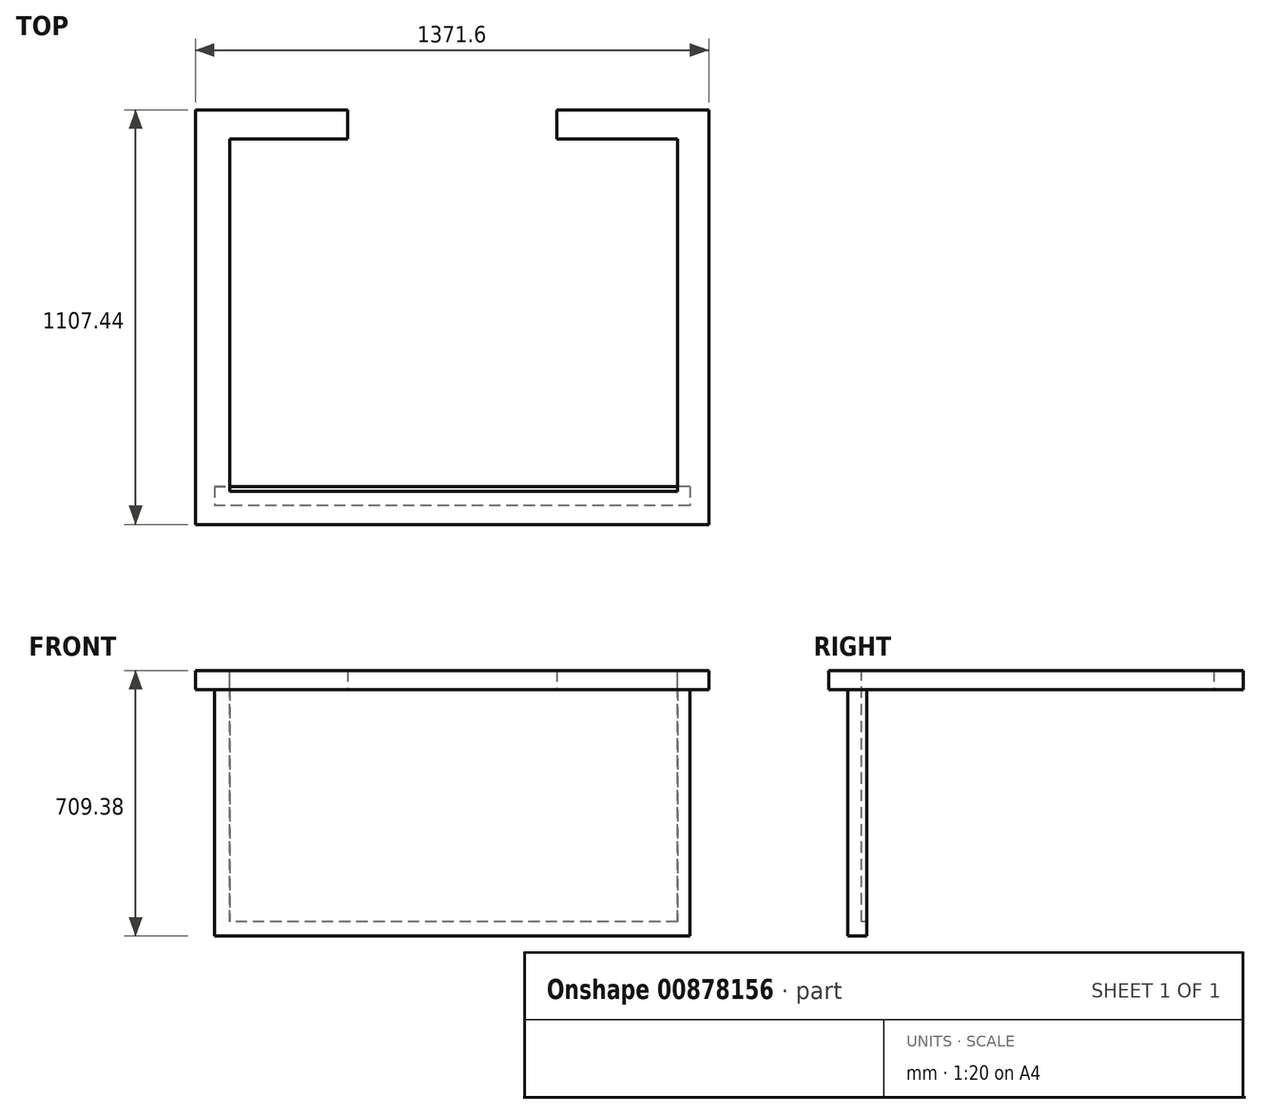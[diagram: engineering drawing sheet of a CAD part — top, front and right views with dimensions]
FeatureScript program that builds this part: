
annotation { "Feature Type Name" : "Feature", "Feature Type Description" : "" }
export const myFeature = defineFeature(function(context is Context, id is Id, definition is map)
    precondition{}
    {
        {
            var Q0;
            Q0=qCreatedBy(makeId("Front.planeOp"),FACE);
            var sketch = newSketch(context, id + "F0", { "sketchPlane" : qUnion([Q0])});
            skLineSegment(sketch, "E0", {"start": v(0, 0) * mm, "end": v(-1270, 0) * mm});
            skLineSegment(sketch, "E1", {"start": v(-1270, 0) * mm, "end": v(-1270, 658.58) * mm});
            skLineSegment(sketch, "E2", {"start": v(-1270, 658.58) * mm, "end": v(-1320.8, 658.58) * mm});
            skLineSegment(sketch, "E3", {"start": v(-1320.8, 658.58) * mm, "end": v(-1320.8, 709.38) * mm});
            skLineSegment(sketch, "E4", {"start": v(-1320.8, 709.38) * mm, "end": v(50.8, 709.38) * mm});
            skLineSegment(sketch, "E5", {"start": v(50.8, 709.38) * mm, "end": v(50.8, 658.58) * mm});
            skLineSegment(sketch, "E6", {"start": v(50.8, 658.58) * mm, "end": v(0, 658.58) * mm});
            skLineSegment(sketch, "E7", {"start": v(0, 658.58) * mm, "end": v(0, 0) * mm});
            skLineSegment(sketch, "E8", {"start": v(0, 658.58) * mm, "end": v(0, 709.38) * mm});
            skLineSegment(sketch, "E9", {"start": v(-1270, 658.58) * mm, "end": v(-1270, 709.38) * mm});
            skSolve(sketch);
        }
        {
            var Q0;
            Q0=makeQuery(id+"F0.imprint","IMPRINT",FACE,{"disambiguationData":[TD([[makeQuery(id+"F0.imprint","IMPRINT",EDGE,{"derivedFrom":sQuery(id+"F0.wireOp",EDGE,"E2")}),-1.0]])]});
            var Q1;
            {var subQ0=sQuery(id+"F0.wireOp",EDGE,"E5");Q1=makeQuery(id+"F0.imprint","IMPRINT",FACE,{"disambiguationData":[TD([[makeQuery(id+"F0.imprint","IMPRINT",EDGE,{"derivedFrom":subQ0}),-1.0]])]});}
            var Q2;
            Q2=makeQuery(id+"F0.imprint","IMPRINT",FACE,{"disambiguationData":[TD([[makeQuery(id+"F0.imprint","IMPRINT",EDGE,{"derivedFrom":sQuery(id+"F0.wireOp",EDGE,"E0")}),-1.0]])]});
            extrude(context, id + "F1", {"entities" : qUnion([Q0, Q1, Q2]), "oppositeDirection" : true, "depth" : 1005.84 * mm, "offsetDistance" : 25.4 * mm});
        }
        {
            var Q0;
            Q0=makeQuery(id+"F1.opExtrude","CAP_FACE",FACE,{"disambiguationData":[OSD([sQuery(id+"F0.wireOp",EDGE,"E0"),sQuery(id+"F0.wireOp",EDGE,"E1"),sQuery(id+"F0.wireOp",EDGE,"E2"),sQuery(id+"F0.wireOp",EDGE,"E3"),sQuery(id+"F0.wireOp",EDGE,"E4"),sQuery(id+"F0.wireOp",EDGE,"E5"),sQuery(id+"F0.wireOp",EDGE,"E6"),sQuery(id+"F0.wireOp",EDGE,"E7")])],"isStart":false});
            var sketch = newSketch(context, id + "F2", { "sketchPlane" : qUnion([Q0])});
            skLineSegment(sketch, "E10", {"start": v(-50.8, 658.58) * mm, "end": v(355.6, 658.58) * mm});
            skLineSegment(sketch, "E11", {"start": v(355.6, 658.58) * mm, "end": v(355.6, 709.38) * mm});
            skLineSegment(sketch, "E12", {"start": v(355.6, 709.38) * mm, "end": v(-50.8, 709.38) * mm});
            skLineSegment(sketch, "E13", {"start": v(-50.8, 709.38) * mm, "end": v(-50.8, 658.58) * mm});
            skLineSegment(sketch, "E14", {"start": v(1320.8, 658.58) * mm, "end": v(914.4, 658.58) * mm});
            skLineSegment(sketch, "E15", {"start": v(914.4, 658.58) * mm, "end": v(914.4, 709.38) * mm});
            skLineSegment(sketch, "E16", {"start": v(914.4, 709.38) * mm, "end": v(1320.8, 709.38) * mm});
            skLineSegment(sketch, "E17", {"start": v(1320.8, 709.38) * mm, "end": v(1320.8, 658.58) * mm});
            skSolve(sketch);
        }
        {
            var Q0;
            {var subQ0=sQuery(id+"F2.wireOp",EDGE,"E15");Q0=makeQuery(id+"F2.imprint","IMPRINT",FACE,{"disambiguationData":[TD([[makeQuery(id+"F2.imprint","IMPRINT",EDGE,{"derivedFrom":subQ0}),-1.0]])]});}
            var Q1;
            {var subQ0=sQuery(id+"F2.wireOp",EDGE,"E11");Q1=makeQuery(id+"F2.imprint","IMPRINT",FACE,{"disambiguationData":[TD([[makeQuery(id+"F2.imprint","IMPRINT",EDGE,{"derivedFrom":subQ0}),1.0]])]});}
            extrude(context, id + "F3", {"entities" : qUnion([Q0, Q1]), "operationType" : NewBodyOperationType.ADD, "depth" : 50.8 * mm, "offsetDistance" : 25.4 * mm});
        }
        {
            var Q0;
            Q0=makeQuery(id+"F1.opExtrude","CAP_FACE",FACE,{"disambiguationData":[OSD([sQuery(id+"F0.wireOp",EDGE,"E0"),sQuery(id+"F0.wireOp",EDGE,"E1"),sQuery(id+"F0.wireOp",EDGE,"E2"),sQuery(id+"F0.wireOp",EDGE,"E3"),sQuery(id+"F0.wireOp",EDGE,"E4"),sQuery(id+"F0.wireOp",EDGE,"E5"),sQuery(id+"F0.wireOp",EDGE,"E6"),sQuery(id+"F0.wireOp",EDGE,"E7")])],"isStart":true});
            var sketch = newSketch(context, id + "F4", { "sketchPlane" : qUnion([Q0])});
            skLineSegment(sketch, "E18", {"start": v(-1320.8, 658.58) * mm, "end": v(50.8, 658.58) * mm});
            skLineSegment(sketch, "E19", {"start": v(50.8, 658.58) * mm, "end": v(50.8, 709.38) * mm});
            skLineSegment(sketch, "E20", {"start": v(50.8, 709.38) * mm, "end": v(-1320.8, 709.38) * mm});
            skLineSegment(sketch, "E21", {"start": v(-1320.8, 709.38) * mm, "end": v(-1320.8, 658.58) * mm});
            skSolve(sketch);
        }
        {
            var Q0;
            Q0 = qSketchRegion(id + "F4", true);
            extrude(context, id + "F5", {"entities" : qUnion([Q0]), "operationType" : NewBodyOperationType.ADD, "depth" : 50.8 * mm, "offsetDistance" : 25.4 * mm});
        }
        {
            var Q0;
            Q0=makeQuery(id+"F5.boolean.opBoolean","MERGE",FACE,{"derivedFrom":[makeQuery(id+"F3.boolean.opBoolean","MERGE",FACE,{"derivedFrom":[makeQuery(id+"F1.opExtrude","SWEPT_FACE",FACE,{"disambiguationData":[OSD([sQuery(id+"F0.wireOp",EDGE,"E4")])]}),makeQuery(id+"F3.opExtrude","SWEPT_FACE",FACE,{"disambiguationData":[OSD([sQuery(id+"F2.wireOp",EDGE,"E12")])]}),makeQuery(id+"F3.opExtrude","SWEPT_FACE",FACE,{"disambiguationData":[OSD([sQuery(id+"F2.wireOp",EDGE,"E16")])]})]}),makeQuery(id+"F5.opExtrude","SWEPT_FACE",FACE,{"disambiguationData":[OSD([sQuery(id+"F4.wireOp",EDGE,"E20")])]})]});
            var sketch = newSketch(context, id + "F6", { "sketchPlane" : qUnion([Q0])});
            skPoint(sketch, "E22.0", {"position": v(50.8, -50.8) * mm});
            skPoint(sketch, "E23.0", {"position": v(0, 0) * mm});
            skSolve(sketch);
        }
        {
            var Q0;
            {var subQ1=sQuery(id+"F2.wireOp",EDGE,"E12");Q0=makeQuery(id+"F6.imprint","IMPRINT",FACE,{"disambiguationData":[TD([[makeQuery(id+"F6.imprint","IMPRINT",EDGE,{"derivedFrom":makeQuery(id+"F3.opExtrude","CAP_EDGE",EDGE,{"disambiguationData":[OSD([subQ1])],"isStart":false})}),-1.0]])]});}
            var sketch = newSketch(context, id + "F7", { "sketchPlane" : qUnion([Q0])});
            skLineSegment(sketch, "E24", {"start": v(-1271.6, 1006.87) * mm, "end": v(0, 1006.87) * mm});
            skLineSegment(sketch, "E25", {"start": v(0, 1006.87) * mm, "end": v(0, 0) * mm});
            skLineSegment(sketch, "E26", {"start": v(0, 0) * mm, "end": v(-1269.46, 0) * mm});
            skLineSegment(sketch, "E27", {"start": v(-1269.46, 0) * mm, "end": v(-1271.6, 1006.87) * mm});
            skSolve(sketch);
        }
        {
            var Q0;
            {var subQ5=sQuery(id+"F7.wireOp",EDGE,"E25");Q0=makeQuery(id+"F7.imprint","IMPRINT",FACE,{"disambiguationData":[TD([[makeQuery(id+"F7.imprint","IMPRINT",EDGE,{"derivedFrom":subQ5}),-1.0]])]});}
            var sketch = newSketch(context, id + "F8", { "sketchPlane" : qUnion([Q0])});
            skLineSegment(sketch, "E28.bottom", {"start": v(-1228.49, 978.37) * mm, "end": v(-32.9, 978.37) * mm});
            skLineSegment(sketch, "E28.top", {"start": v(-1228.49, 37.75) * mm, "end": v(-32.9, 37.75) * mm});
            skLineSegment(sketch, "E28.left", {"start": v(-1228.49, 978.37) * mm, "end": v(-1228.49, 37.75) * mm});
            skLineSegment(sketch, "E28.right", {"start": v(-32.9, 978.37) * mm, "end": v(-32.9, 37.75) * mm});
            skSolve(sketch);
        }
        {
            var Q0;
            Q0 = qSketchRegion(id + "F8", true);
            extrude(context, id + "F9", {"entities" : qUnion([Q0]), "operationType" : NewBodyOperationType.REMOVE, "oppositeDirection" : true, "depth" : 670.56 * mm, "offsetDistance" : 25.4 * mm});
        }
        {
            var Q0;
            Q0=makeQuery(id+"F1.opExtrude","CAP_FACE",FACE,{"disambiguationData":[OSD([sQuery(id+"F0.wireOp",EDGE,"E0"),sQuery(id+"F0.wireOp",EDGE,"E1"),sQuery(id+"F0.wireOp",EDGE,"E2"),sQuery(id+"F0.wireOp",EDGE,"E3"),sQuery(id+"F0.wireOp",EDGE,"E4"),sQuery(id+"F0.wireOp",EDGE,"E5"),sQuery(id+"F0.wireOp",EDGE,"E6"),sQuery(id+"F0.wireOp",EDGE,"E7")])],"isStart":false});
            var sketch = newSketch(context, id + "F10", { "sketchPlane" : qUnion([Q0])});
            skLineSegment(sketch, "E29", {"start": v(355.6, 658.58) * mm, "end": v(355.6, 113.77) * mm});
            skLineSegment(sketch, "E30", {"start": v(355.6, 113.77) * mm, "end": v(914.4, 113.77) * mm});
            skLineSegment(sketch, "E31", {"start": v(914.4, 113.77) * mm, "end": v(914.4, 658.58) * mm});
            skLineSegment(sketch, "E32", {"start": v(914.4, 658.58) * mm, "end": v(914.4, 709.38) * mm});
            skLineSegment(sketch, "E33", {"start": v(914.4, 709.38) * mm, "end": v(355.6, 709.38) * mm});
            skLineSegment(sketch, "E34", {"start": v(355.6, 709.38) * mm, "end": v(355.6, 658.58) * mm});
            skSolve(sketch);
        }
        {
            var Q0;
            Q0 = qSketchRegion(id + "F10", true);
            var Q1;
            Q1=makeQuery(id+"F10.imprint","IMPRINT",FACE,{"disambiguationData":[TD([[makeQuery(id+"F10.imprint","IMPRINT",EDGE,{"derivedFrom":sQuery(id+"F10.wireOp",EDGE,"E29")}),-1.0]])]});
            extrude(context, id + "F11", {"entities" : qUnion([Q0, Q1]), "operationType" : NewBodyOperationType.REMOVE, "oppositeDirection" : true, "depth" : 955.04 * mm, "offsetDistance" : 25.4 * mm});
        }
    });
